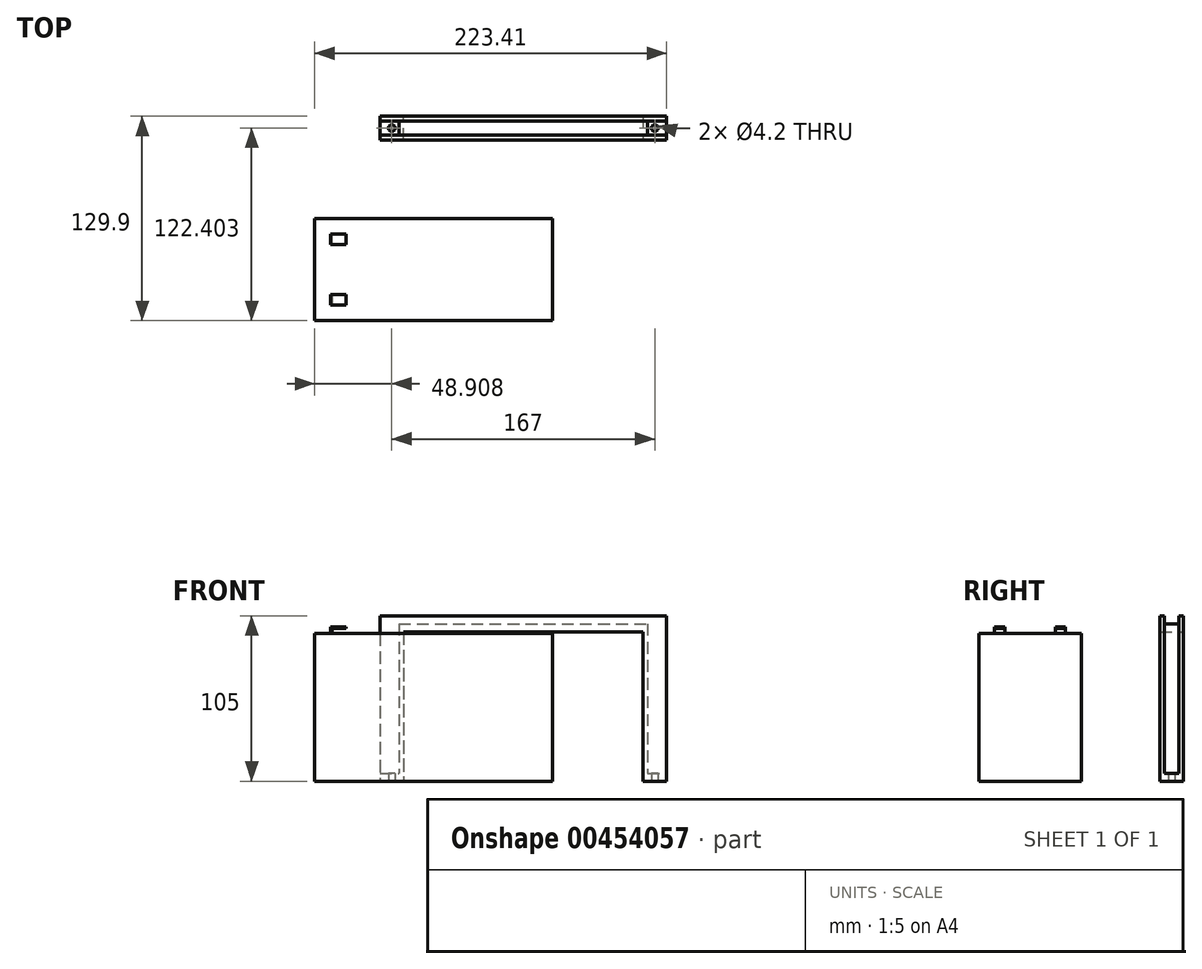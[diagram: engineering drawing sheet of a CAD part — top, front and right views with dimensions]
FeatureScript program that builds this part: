
annotation { "Feature Type Name" : "Feature", "Feature Type Description" : "" }
export const myFeature = defineFeature(function(context is Context, id is Id, definition is map)
    precondition{}
    {
        {
            var Q0;
            Q0=qCreatedBy(makeId("Top.planeOp"),FACE);
            var sketch = newSketch(context, id + "F0", { "sketchPlane" : qUnion([Q0])});
            skLineSegment(sketch, "E0.bottom", {"start": v(-104.43, 14.84) * mm, "end": v(46.57, 14.84) * mm});
            skLineSegment(sketch, "E0.top", {"start": v(-104.43, -50.16) * mm, "end": v(46.57, -50.16) * mm});
            skLineSegment(sketch, "E0.left", {"start": v(-104.43, 14.84) * mm, "end": v(-104.43, -50.16) * mm});
            skLineSegment(sketch, "E0.right", {"start": v(46.57, 14.84) * mm, "end": v(46.57, -50.16) * mm});
            skSolve(sketch);
        }
        {
            var Q0;
            Q0 = qSketchRegion(id + "F0", true);
            extrude(context, id + "F1", {"entities" : qUnion([Q0]), "depth" : 94 * mm, "offsetDistance" : 25 * mm});
        }
        {
            var Q0;
            Q0=makeQuery(id+"F1.opExtrude","CAP_FACE",FACE,{"disambiguationData":[OSD([sQuery(id+"F0.wireOp",EDGE,"E0.bottom"),sQuery(id+"F0.wireOp",EDGE,"E0.top"),sQuery(id+"F0.wireOp",EDGE,"E0.left"),sQuery(id+"F0.wireOp",EDGE,"E0.right")])],"isStart":false});
            var sketch = newSketch(context, id + "F2", { "sketchPlane" : qUnion([Q0])});
            skLineSegment(sketch, "E1", {"start": v(-94.43, -40.16) * mm, "end": v(-94.43, -33.66) * mm});
            skLineSegment(sketch, "E2", {"start": v(-94.43, -33.66) * mm, "end": v(-93.43, -33.66) * mm});
            skLineSegment(sketch, "E3", {"start": v(-93.43, -33.66) * mm, "end": v(-93.43, -40.16) * mm});
            skLineSegment(sketch, "E4", {"start": v(-93.43, -40.16) * mm, "end": v(-94.43, -40.16) * mm});
            skLineSegment(sketch, "E5", {"start": v(-94.43, 4.84) * mm, "end": v(-94.43, -1.66) * mm});
            skLineSegment(sketch, "E6", {"start": v(-94.43, -1.66) * mm, "end": v(-93.43, -1.66) * mm});
            skLineSegment(sketch, "E7", {"start": v(-93.43, -1.66) * mm, "end": v(-93.43, 4.84) * mm});
            skLineSegment(sketch, "E8", {"start": v(-93.43, 4.84) * mm, "end": v(-94.43, 4.84) * mm});
            skSolve(sketch);
        }
        {
            var Q0;
            Q0 = qSketchRegion(id + "F2", true);
            extrude(context, id + "F3", {"entities" : qUnion([Q0]), "operationType" : NewBodyOperationType.ADD, "depth" : 3 * mm, "offsetDistance" : 25 * mm});
        }
        {
            var Q0;
            Q0=makeQuery(id+"F3.opExtrude","CAP_FACE",FACE,{"disambiguationData":[OSD([sQuery(id+"F2.wireOp",EDGE,"E1"),sQuery(id+"F2.wireOp",EDGE,"E2"),sQuery(id+"F2.wireOp",EDGE,"E3"),sQuery(id+"F2.wireOp",EDGE,"E4")])],"isStart":false});
            var sketch = newSketch(context, id + "F4", { "sketchPlane" : qUnion([Q0])});
            skLineSegment(sketch, "E9", {"start": v(-94.43, -40.16) * mm, "end": v(-94.43, -33.66) * mm});
            skLineSegment(sketch, "E10", {"start": v(-94.43, -33.66) * mm, "end": v(-84.43, -33.66) * mm});
            skLineSegment(sketch, "E11", {"start": v(-84.43, -33.66) * mm, "end": v(-84.43, -40.16) * mm});
            skLineSegment(sketch, "E12", {"start": v(-84.43, -40.16) * mm, "end": v(-94.43, -40.16) * mm});
            skSolve(sketch);
        }
        {
            var Q0;
            Q0 = qSketchRegion(id + "F4", true);
            extrude(context, id + "F5", {"entities" : qUnion([Q0]), "operationType" : NewBodyOperationType.ADD, "depth" : 1 * mm, "offsetDistance" : 25 * mm});
        }
        {
            var Q0;
            Q0=makeQuery(id+"F3.opExtrude","CAP_FACE",FACE,{"disambiguationData":[OSD([sQuery(id+"F2.wireOp",EDGE,"E5"),sQuery(id+"F2.wireOp",EDGE,"E6"),sQuery(id+"F2.wireOp",EDGE,"E7"),sQuery(id+"F2.wireOp",EDGE,"E8")])],"isStart":false});
            var sketch = newSketch(context, id + "F6", { "sketchPlane" : qUnion([Q0])});
            skLineSegment(sketch, "E13", {"start": v(-94.43, 4.84) * mm, "end": v(-84.43, 4.84) * mm});
            skLineSegment(sketch, "E14", {"start": v(-84.43, 4.84) * mm, "end": v(-84.43, -1.66) * mm});
            skLineSegment(sketch, "E15", {"start": v(-84.43, -1.66) * mm, "end": v(-94.43, -1.66) * mm});
            skLineSegment(sketch, "E16", {"start": v(-94.43, -1.66) * mm, "end": v(-94.43, 4.84) * mm});
            skSolve(sketch);
        }
        {
            var Q0;
            Q0 = qSketchRegion(id + "F6", true);
            extrude(context, id + "F7", {"entities" : qUnion([Q0]), "operationType" : NewBodyOperationType.ADD, "depth" : 1 * mm, "offsetDistance" : 25 * mm});
        }
        {
            var Q0;
            Q0=qCreatedBy(makeId("Top.planeOp"),FACE);
            var sketch = newSketch(context, id + "F8", { "sketchPlane" : qUnion([Q0])});
            skLineSegment(sketch, "E17", {"start": v(-63.02, 79.74) * mm, "end": v(-63.02, 64.74) * mm});
            skLineSegment(sketch, "E18", {"start": v(-63.02, 64.74) * mm, "end": v(-48.02, 64.74) * mm});
            skLineSegment(sketch, "E19", {"start": v(-48.02, 64.74) * mm, "end": v(-48.02, 79.74) * mm});
            skLineSegment(sketch, "E20", {"start": v(-48.02, 79.74) * mm, "end": v(-63.02, 79.74) * mm});
            skCircle(sketch, "E21", {"center": v(-55.52, 72.24) * mm, "radius": 2.1 * mm});
            skLineSegment(sketch, "E22", {"start": v(103.98, 79.74) * mm, "end": v(103.98, 64.74) * mm});
            skLineSegment(sketch, "E23", {"start": v(103.98, 64.74) * mm, "end": v(118.98, 64.74) * mm});
            skLineSegment(sketch, "E24", {"start": v(118.98, 64.74) * mm, "end": v(118.98, 79.74) * mm});
            skLineSegment(sketch, "E25", {"start": v(118.98, 79.74) * mm, "end": v(103.98, 79.74) * mm});
            skCircle(sketch, "E26", {"center": v(111.48, 72.24) * mm, "radius": 2.1 * mm});
            skSolve(sketch);
        }
        {
            var Q0;
            Q0 = qSketchRegion(id + "F8", true);
            extrude(context, id + "F9", {"entities" : qUnion([Q0]), "depth" : 5 * mm, "offsetDistance" : 25 * mm});
        }
        {
            var Q0;
            Q0=makeQuery(id+"F9.opExtrude","CAP_FACE",FACE,{"disambiguationData":[OSD([sQuery(id+"F8.wireOp",EDGE,"E17"),sQuery(id+"F8.wireOp",EDGE,"E18"),sQuery(id+"F8.wireOp",EDGE,"E19"),sQuery(id+"F8.wireOp",EDGE,"E20"),sQuery(id+"F8.wireOp",EDGE,"E21")])],"isStart":false});
            var sketch = newSketch(context, id + "F10", { "sketchPlane" : qUnion([Q0])});
            skLineSegment(sketch, "E27", {"start": v(-63.02, 79.74) * mm, "end": v(-48.02, 79.74) * mm});
            skLineSegment(sketch, "E28", {"start": v(-48.02, 79.74) * mm, "end": v(-48.02, 64.74) * mm});
            skLineSegment(sketch, "E29", {"start": v(-48.02, 64.74) * mm, "end": v(-63.02, 64.74) * mm});
            skLineSegment(sketch, "E30", {"start": v(-63.02, 64.74) * mm, "end": v(-63.02, 67.74) * mm});
            skLineSegment(sketch, "E31", {"start": v(-63.02, 67.74) * mm, "end": v(-51.02, 67.74) * mm});
            skLineSegment(sketch, "E32", {"start": v(-51.02, 67.74) * mm, "end": v(-51.02, 76.74) * mm});
            skLineSegment(sketch, "E33", {"start": v(-51.02, 76.74) * mm, "end": v(-63.02, 76.74) * mm});
            skLineSegment(sketch, "E34", {"start": v(-63.02, 76.74) * mm, "end": v(-63.02, 79.74) * mm});
            skSolve(sketch);
        }
        {
            var Q0;
            Q0 = qSketchRegion(id + "F10", true);
            extrude(context, id + "F11", {"entities" : qUnion([Q0]), "operationType" : NewBodyOperationType.ADD, "depth" : 90 * mm, "offsetDistance" : 25 * mm});
        }
        {
            var Q0;
            Q0=makeQuery(id+"F9.opExtrude","CAP_FACE",FACE,{"disambiguationData":[OSD([sQuery(id+"F8.wireOp",EDGE,"E22"),sQuery(id+"F8.wireOp",EDGE,"E23"),sQuery(id+"F8.wireOp",EDGE,"E24"),sQuery(id+"F8.wireOp",EDGE,"E25"),sQuery(id+"F8.wireOp",EDGE,"E26")])],"isStart":false});
            var sketch = newSketch(context, id + "F12", { "sketchPlane" : qUnion([Q0])});
            skLineSegment(sketch, "E35", {"start": v(118.98, 64.74) * mm, "end": v(103.98, 64.74) * mm});
            skLineSegment(sketch, "E36", {"start": v(103.98, 64.74) * mm, "end": v(103.98, 79.74) * mm});
            skLineSegment(sketch, "E37", {"start": v(103.98, 79.74) * mm, "end": v(118.98, 79.74) * mm});
            skLineSegment(sketch, "E38", {"start": v(118.98, 79.74) * mm, "end": v(118.98, 76.74) * mm});
            skLineSegment(sketch, "E39", {"start": v(118.98, 76.74) * mm, "end": v(106.98, 76.74) * mm});
            skLineSegment(sketch, "E40", {"start": v(106.98, 76.74) * mm, "end": v(106.98, 67.74) * mm});
            skLineSegment(sketch, "E41", {"start": v(106.98, 67.74) * mm, "end": v(118.98, 67.74) * mm});
            skLineSegment(sketch, "E42", {"start": v(118.98, 67.74) * mm, "end": v(118.98, 64.74) * mm});
            skSolve(sketch);
        }
        {
            var Q0;
            Q0 = qSketchRegion(id + "F12", true);
            extrude(context, id + "F13", {"entities" : qUnion([Q0]), "operationType" : NewBodyOperationType.ADD, "depth" : 90 * mm, "offsetDistance" : 25 * mm});
        }
        {
            var Q0;
            Q0=makeQuery(id+"F11.opExtrude","CAP_FACE",FACE,{"disambiguationData":[OSD([sQuery(id+"F10.wireOp",EDGE,"E27"),sQuery(id+"F10.wireOp",EDGE,"E28"),sQuery(id+"F10.wireOp",EDGE,"E29"),sQuery(id+"F10.wireOp",EDGE,"E30"),sQuery(id+"F10.wireOp",EDGE,"E31"),sQuery(id+"F10.wireOp",EDGE,"E32"),sQuery(id+"F10.wireOp",EDGE,"E33"),sQuery(id+"F10.wireOp",EDGE,"E34")])],"isStart":false});
            var sketch = newSketch(context, id + "F14", { "sketchPlane" : qUnion([Q0])});
            skLineSegment(sketch, "E43", {"start": v(-48.02, 79.74) * mm, "end": v(103.98, 79.74) * mm});
            skLineSegment(sketch, "E44", {"start": v(103.98, 64.74) * mm, "end": v(-48.02, 64.74) * mm});
            skLineSegment(sketch, "E45", {"start": v(103.98, 79.74) * mm, "end": v(118.98, 79.74) * mm});
            skLineSegment(sketch, "E46", {"start": v(118.98, 79.74) * mm, "end": v(118.98, 76.74) * mm});
            skLineSegment(sketch, "E47", {"start": v(118.98, 76.74) * mm, "end": v(106.98, 76.74) * mm});
            skLineSegment(sketch, "E48", {"start": v(106.98, 76.74) * mm, "end": v(106.98, 67.74) * mm});
            skLineSegment(sketch, "E49", {"start": v(106.98, 67.74) * mm, "end": v(118.98, 67.74) * mm});
            skLineSegment(sketch, "E50", {"start": v(118.98, 67.74) * mm, "end": v(118.98, 64.74) * mm});
            skLineSegment(sketch, "E51", {"start": v(118.98, 64.74) * mm, "end": v(103.98, 64.74) * mm});
            skLineSegment(sketch, "E52", {"start": v(-48.02, 64.74) * mm, "end": v(-63.02, 64.74) * mm});
            skLineSegment(sketch, "E53", {"start": v(-63.02, 64.74) * mm, "end": v(-63.02, 67.74) * mm});
            skLineSegment(sketch, "E54", {"start": v(-63.02, 67.74) * mm, "end": v(-51.02, 67.74) * mm});
            skLineSegment(sketch, "E55", {"start": v(-51.02, 67.74) * mm, "end": v(-51.02, 76.74) * mm});
            skLineSegment(sketch, "E56", {"start": v(-51.02, 76.74) * mm, "end": v(-63.02, 76.74) * mm});
            skLineSegment(sketch, "E57", {"start": v(-63.02, 76.74) * mm, "end": v(-63.02, 79.74) * mm});
            skLineSegment(sketch, "E58", {"start": v(-63.02, 79.74) * mm, "end": v(-48.02, 79.74) * mm});
            skSolve(sketch);
        }
        {
            var Q0;
            Q0 = qSketchRegion(id + "F14", true);
            extrude(context, id + "F15", {"entities" : qUnion([Q0]), "operationType" : NewBodyOperationType.ADD, "depth" : 5 * mm, "offsetDistance" : 25 * mm});
        }
        {
            var Q0;
            Q0=makeQuery(id+"F15.opExtrude","CAP_FACE",FACE,{"disambiguationData":[OSD([sQuery(id+"F14.wireOp",EDGE,"E43"),sQuery(id+"F14.wireOp",EDGE,"E44"),sQuery(id+"F14.wireOp",EDGE,"E45"),sQuery(id+"F14.wireOp",EDGE,"E46"),sQuery(id+"F14.wireOp",EDGE,"E47"),sQuery(id+"F14.wireOp",EDGE,"E48"),sQuery(id+"F14.wireOp",EDGE,"E49"),sQuery(id+"F14.wireOp",EDGE,"E50"),sQuery(id+"F14.wireOp",EDGE,"E51"),sQuery(id+"F14.wireOp",EDGE,"E52"),sQuery(id+"F14.wireOp",EDGE,"E53"),sQuery(id+"F14.wireOp",EDGE,"E54"),sQuery(id+"F14.wireOp",EDGE,"E55"),sQuery(id+"F14.wireOp",EDGE,"E56"),sQuery(id+"F14.wireOp",EDGE,"E57"),sQuery(id+"F14.wireOp",EDGE,"E58")])],"isStart":false});
            var sketch = newSketch(context, id + "F16", { "sketchPlane" : qUnion([Q0])});
            skLineSegment(sketch, "E59", {"start": v(118.98, 79.74) * mm, "end": v(-63.02, 79.74) * mm});
            skLineSegment(sketch, "E60", {"start": v(-63.02, 79.74) * mm, "end": v(-63.02, 76.74) * mm});
            skLineSegment(sketch, "E61", {"start": v(-63.02, 76.74) * mm, "end": v(118.98, 76.74) * mm});
            skLineSegment(sketch, "E62", {"start": v(118.98, 76.74) * mm, "end": v(118.98, 79.74) * mm});
            skLineSegment(sketch, "E63", {"start": v(118.98, 64.74) * mm, "end": v(-63.02, 64.74) * mm});
            skLineSegment(sketch, "E64", {"start": v(-63.02, 64.74) * mm, "end": v(-63.02, 67.74) * mm});
            skLineSegment(sketch, "E65", {"start": v(-63.02, 67.74) * mm, "end": v(118.98, 67.74) * mm});
            skLineSegment(sketch, "E66", {"start": v(118.98, 67.74) * mm, "end": v(118.98, 64.74) * mm});
            skSolve(sketch);
        }
        {
            var Q0;
            Q0 = qSketchRegion(id + "F16", true);
            extrude(context, id + "F17", {"entities" : qUnion([Q0]), "operationType" : NewBodyOperationType.ADD, "depth" : 5 * mm, "offsetDistance" : 25 * mm});
        }
    });
